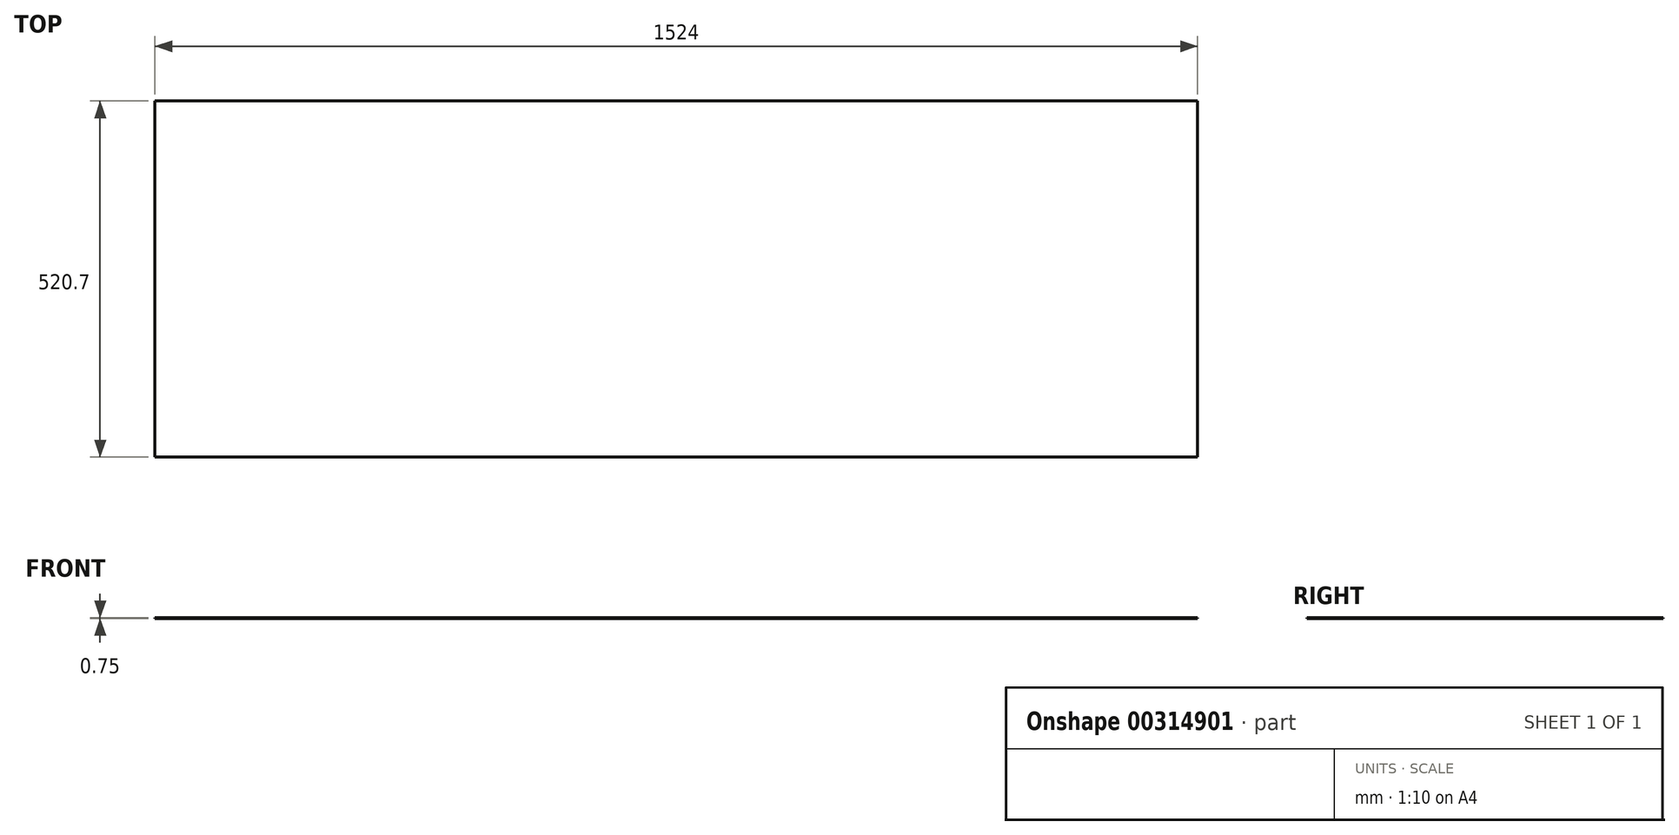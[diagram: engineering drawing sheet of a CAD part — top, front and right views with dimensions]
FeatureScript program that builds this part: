
annotation { "Feature Type Name" : "Feature", "Feature Type Description" : "" }
export const myFeature = defineFeature(function(context is Context, id is Id, definition is map)
    precondition{}
    {
        {
            assignVariable(context, id + "F0", {"name" : "Thickness", "anyValue" : .75});
        }
        {
            var Q0;
            Q0=qCreatedBy(makeId("Top.planeOp"),FACE);
            var sketch = newSketch(context, id + "F1", { "sketchPlane" : qUnion([Q0])});
            skLineSegment(sketch, "E0.bottom", {"start": v(-762, 260.35) * mm, "end": v(762, 260.35) * mm});
            skLineSegment(sketch, "E0.top", {"start": v(-762, -260.35) * mm, "end": v(762, -260.35) * mm});
            skLineSegment(sketch, "E0.left", {"start": v(-762, 260.35) * mm, "end": v(-762, -260.35) * mm});
            skLineSegment(sketch, "E0.right", {"start": v(762, 260.35) * mm, "end": v(762, -260.35) * mm});
            skPoint(sketch, "E0.middle", {"position": v(0, 0) * mm});
            skSolve(sketch);
        }
        {
            var Q0;
            Q0=makeQuery(id+"F1.imprint","IMPRINT",FACE,{"disambiguationData":[TD([[makeQuery(id+"F1.imprint","IMPRINT",EDGE,{"derivedFrom":sQuery(id+"F1.wireOp",EDGE,"E0.bottom")}),-1.0]])]});
            extrude(context, id + "F2", {"entities" : qUnion([Q0]), "oppositeDirection" : true, "depth" : (getVariable(context, 'Thickness')) * mm});
        }
    });
